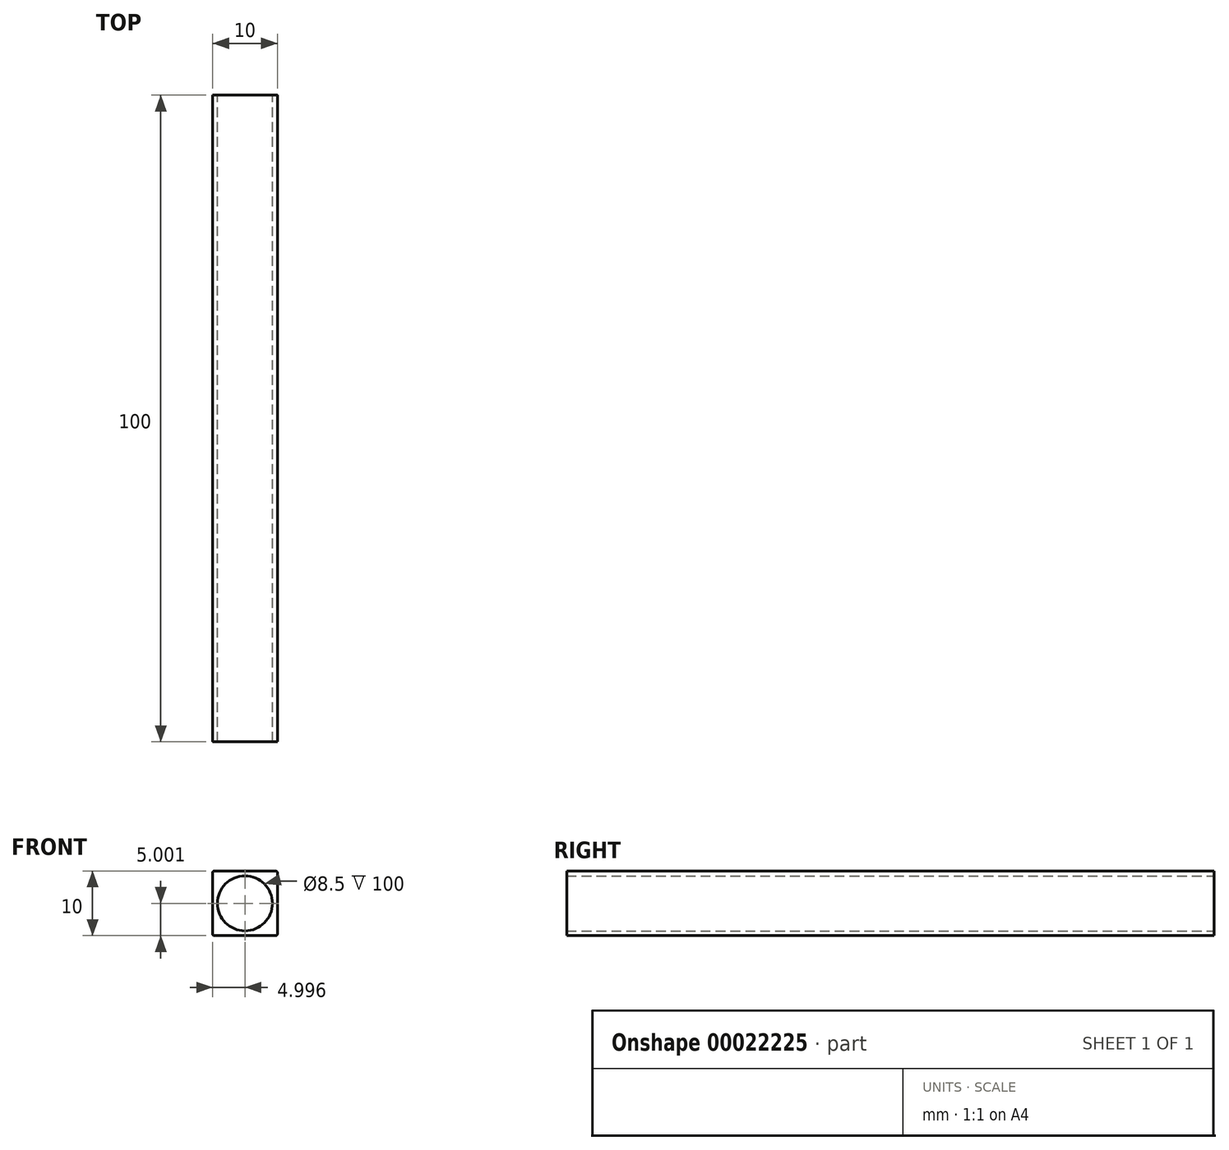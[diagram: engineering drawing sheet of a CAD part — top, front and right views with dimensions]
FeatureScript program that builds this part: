
annotation { "Feature Type Name" : "Feature", "Feature Type Description" : "" }
export const myFeature = defineFeature(function(context is Context, id is Id, definition is map)
    precondition{}
    {
        {
            var Q0;
            Q0=qCreatedBy(makeId("Front.planeOp"),FACE);
            var sketch = newSketch(context, id + "F0", { "sketchPlane" : qUnion([Q0])});
            skLineSegment(sketch, "E0.bottom", {"start": v(0.42, 11.58) * mm, "end": v(9.92, 11.58) * mm});
            skLineSegment(sketch, "E0.top", {"start": v(0.42, 1.58) * mm, "end": v(9.92, 1.58) * mm});
            skLineSegment(sketch, "E0.left", {"start": v(0.17, 11.33) * mm, "end": v(0.17, 1.83) * mm});
            skLineSegment(sketch, "E0.right", {"start": v(10.17, 11.33) * mm, "end": v(10.17, 1.83) * mm});
            skLineSegment(sketch, "E1", {"start": v(5.17, 11.58) * mm, "end": v(5.17, 1.58) * mm, "construction": true});
            skLineSegment(sketch, "E2", {"start": v(0.17, 6.58) * mm, "end": v(10.17, 6.58) * mm, "construction": true});
            skCircle(sketch, "E3", {"center": v(5.17, 6.58) * mm, "radius": 4.25 * mm});
            skCircle(sketch, "E4", {"center": v(0.42, 1.83) * mm, "radius": 0.25 * mm});
            skPoint(sketch, "E5.orphan", {"position": v(0.17, 1.58) * mm});
            skCircle(sketch, "E6", {"center": v(9.92, 1.83) * mm, "radius": 0.25 * mm});
            skPoint(sketch, "E7.orphan", {"position": v(10.17, 1.58) * mm});
            skCircle(sketch, "E8", {"center": v(9.92, 11.33) * mm, "radius": 0.25 * mm});
            skPoint(sketch, "E9.orphan", {"position": v(10.17, 11.58) * mm});
            skCircle(sketch, "E10", {"center": v(0.42, 11.33) * mm, "radius": 0.25 * mm});
            skPoint(sketch, "E11.orphan", {"position": v(0.17, 11.58) * mm});
            skSolve(sketch);
        }
        {
            var Q0;
            {var subQ2=sQuery(id+"F0.wireOp",EDGE,"E0.bottom");Q0=makeQuery(id+"F0.imprint","IMPRINT",FACE,{"disambiguationData":[TD([[makeQuery(id+"F0.imprint","IMPRINT",EDGE,{"derivedFrom":subQ2}),-1.0]])]});}
            var Q1;
            {var subQ0=sQuery(id+"F0.wireOp",EDGE,"E10");var subQ2=makeQuery(id+"F0.imprint","INTERSECT",VERTEX,{"derivedFrom":[sQuery(id+"F0.wireOp",EDGE,"E0.bottom"),subQ0]});Q1=makeQuery(id+"F0.imprint","IMPRINT",FACE,{"disambiguationData":[TD([[makeQuery(id+"F0.imprint","IMPRINT",EDGE,{"disambiguationData":[TD([[subQ2,-1.0]])],"derivedFrom":subQ0}),1.0]])]});}
            var Q2;
            {var subQ0=sQuery(id+"F0.wireOp",EDGE,"E4");var subQ2=makeQuery(id+"F0.imprint","INTERSECT",VERTEX,{"derivedFrom":[sQuery(id+"F0.wireOp",EDGE,"E0.top"),subQ0]});Q2=makeQuery(id+"F0.imprint","IMPRINT",FACE,{"disambiguationData":[TD([[makeQuery(id+"F0.imprint","IMPRINT",EDGE,{"disambiguationData":[TD([[subQ2,1.0]])],"derivedFrom":subQ0}),1.0]])]});}
            var Q3;
            {var subQ0=sQuery(id+"F0.wireOp",EDGE,"E8");var subQ2=makeQuery(id+"F0.imprint","INTERSECT",VERTEX,{"derivedFrom":[sQuery(id+"F0.wireOp",EDGE,"E0.bottom"),subQ0]});Q3=makeQuery(id+"F0.imprint","IMPRINT",FACE,{"disambiguationData":[TD([[makeQuery(id+"F0.imprint","IMPRINT",EDGE,{"disambiguationData":[TD([[subQ2,1.0]])],"derivedFrom":subQ0}),1.0]])]});}
            var Q4;
            {var subQ0=sQuery(id+"F0.wireOp",EDGE,"E6");var subQ2=makeQuery(id+"F0.imprint","INTERSECT",VERTEX,{"derivedFrom":[sQuery(id+"F0.wireOp",EDGE,"E0.top"),subQ0]});Q4=makeQuery(id+"F0.imprint","IMPRINT",FACE,{"disambiguationData":[TD([[makeQuery(id+"F0.imprint","IMPRINT",EDGE,{"disambiguationData":[TD([[subQ2,1.0]])],"derivedFrom":subQ0}),1.0]])]});}
            extrude(context, id + "F1", {"entities" : qUnion([Q0, Q1, Q2, Q3, Q4]), "depth" : 100 * mm});
        }
    });
